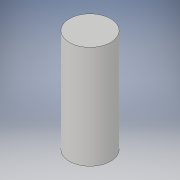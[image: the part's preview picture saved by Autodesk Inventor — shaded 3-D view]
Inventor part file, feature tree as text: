
AUTODESK INVENTOR PART (.ipt)
format: ipt  version: 2019 (Build 230136000, 136)  size: 88,064 bytes
history: native  units: mm
features: extrude x1, sketch x1
ambient origin geometry x8: Origin, YZ Plane, XZ Plane, XY Plane, X Axis, Y Axis, Z Axis, Center Point
bodies: Solid1 (feature_tree)
feature tree (2):
  extrude  "Extrusion1"  Depth=20.0mm TaperAngle=0.0deg
  sketch  "Sketch1"  dims[d0=8.0mm d1=20.0mm d2=0.0mm]
